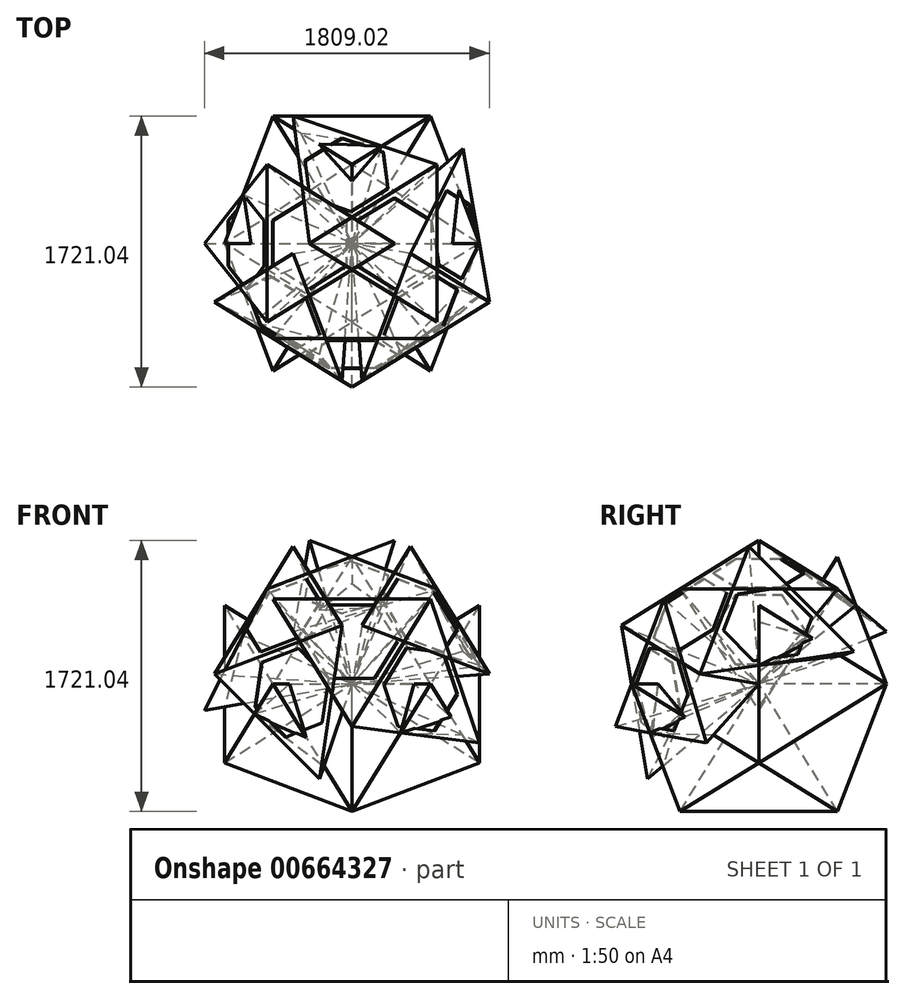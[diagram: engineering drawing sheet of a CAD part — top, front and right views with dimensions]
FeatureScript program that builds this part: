
annotation { "Feature Type Name" : "Feature", "Feature Type Description" : "" }
export const myFeature = defineFeature(function(context is Context, id is Id, definition is map)
    precondition{}
    {
        {
            var Q0;
            Q0=qCreatedBy(makeId("Front.planeOp"),FACE);
            var sketch = newSketch(context, id + "F0", { "sketchPlane" : qUnion([Q0])});
            skLineSegment(sketch, "E0.bottom", {"start": v(-809.02, 500) * mm, "end": v(190.98, 500) * mm, "construction": true});
            skLineSegment(sketch, "E0.top", {"start": v(-809.02, -500) * mm, "end": v(190.98, -500) * mm, "construction": true});
            skLineSegment(sketch, "E0.left", {"start": v(-809.02, 500) * mm, "end": v(-809.02, -500) * mm, "construction": true});
            skLineSegment(sketch, "E0.right", {"start": v(190.98, 500) * mm, "end": v(190.98, -500) * mm, "construction": true});
            skLineSegment(sketch, "E1", {"start": v(190.98, -500) * mm, "end": v(809.02, -500) * mm, "construction": true});
            skArc(sketch, "E2", {"start": v(190.98, 500) * mm, "mid": v(642.04, 87.79) * mm, "end": v(809.02, -500) * mm, "construction": true});
            skLineSegment(sketch, "E3.bottom", {"start": v(809.02, -500) * mm, "end": v(-809.02, -500) * mm});
            skLineSegment(sketch, "E3.top", {"start": v(809.02, 500) * mm, "end": v(-809.02, 500) * mm});
            skLineSegment(sketch, "E3.left", {"start": v(809.02, -500) * mm, "end": v(809.02, 500) * mm});
            skLineSegment(sketch, "E3.right", {"start": v(-809.02, -500) * mm, "end": v(-809.02, 500) * mm});
            skLineSegment(sketch, "E4", {"start": v(0, 0) * mm, "end": v(0, 500) * mm, "construction": true});
            skLineSegment(sketch, "E5", {"start": v(0, 0) * mm, "end": v(-809.02, 0) * mm, "construction": true});
            skSolve(sketch);
        }
        {
            var Q0;
            Q0=qCreatedBy(makeId("Top.planeOp"),FACE);
            var sketch = newSketch(context, id + "F1", { "sketchPlane" : qUnion([Q0])});
            skLineSegment(sketch, "E6.bottom", {"start": v(-500, -809.02) * mm, "end": v(-500, 190.98) * mm, "construction": true});
            skLineSegment(sketch, "E6.top", {"start": v(500, -809.02) * mm, "end": v(500, 190.98) * mm, "construction": true});
            skLineSegment(sketch, "E6.left", {"start": v(-500, -809.02) * mm, "end": v(500, -809.02) * mm, "construction": true});
            skLineSegment(sketch, "E6.right", {"start": v(-500, 190.98) * mm, "end": v(500, 190.98) * mm, "construction": true});
            skLineSegment(sketch, "E7", {"start": v(500, 190.98) * mm, "end": v(500, 809.02) * mm, "construction": true});
            skArc(sketch, "E8", {"start": v(-500, 190.98) * mm, "mid": v(-87.79, 642.04) * mm, "end": v(500, 809.02) * mm, "construction": true});
            skLineSegment(sketch, "E9.bottom", {"start": v(500, 809.02) * mm, "end": v(500, -809.02) * mm});
            skLineSegment(sketch, "E9.top", {"start": v(-500, 809.02) * mm, "end": v(-500, -809.02) * mm});
            skLineSegment(sketch, "E9.left", {"start": v(500, 809.02) * mm, "end": v(-500, 809.02) * mm});
            skLineSegment(sketch, "E9.right", {"start": v(500, -809.02) * mm, "end": v(-500, -809.02) * mm});
            skLineSegment(sketch, "E10", {"start": v(0, 0) * mm, "end": v(-500, 0) * mm, "construction": true});
            skLineSegment(sketch, "E11", {"start": v(0, 0) * mm, "end": v(0, -809.02) * mm, "construction": true});
            skSolve(sketch);
        }
        {
            var Q0;
            Q0=qCreatedBy(makeId("Right.planeOp"),FACE);
            var sketch = newSketch(context, id + "F2", { "sketchPlane" : qUnion([Q0])});
            skLineSegment(sketch, "E12.bottom", {"start": v(-500, -809.02) * mm, "end": v(-500, 190.98) * mm, "construction": true});
            skLineSegment(sketch, "E12.top", {"start": v(500, -809.02) * mm, "end": v(500, 190.98) * mm, "construction": true});
            skLineSegment(sketch, "E12.left", {"start": v(-500, -809.02) * mm, "end": v(500, -809.02) * mm, "construction": true});
            skLineSegment(sketch, "E12.right", {"start": v(-500, 190.98) * mm, "end": v(500, 190.98) * mm, "construction": true});
            skLineSegment(sketch, "E13", {"start": v(500, 190.98) * mm, "end": v(500, 809.02) * mm, "construction": true});
            skArc(sketch, "E14", {"start": v(-500, 190.98) * mm, "mid": v(-87.79, 642.04) * mm, "end": v(500, 809.02) * mm, "construction": true});
            skLineSegment(sketch, "E15.bottom", {"start": v(500, 809.02) * mm, "end": v(500, -809.02) * mm});
            skLineSegment(sketch, "E15.top", {"start": v(-500, 809.02) * mm, "end": v(-500, -809.02) * mm});
            skLineSegment(sketch, "E15.left", {"start": v(500, 809.02) * mm, "end": v(-500, 809.02) * mm});
            skLineSegment(sketch, "E15.right", {"start": v(500, -809.02) * mm, "end": v(-500, -809.02) * mm});
            skLineSegment(sketch, "E16", {"start": v(0, 0) * mm, "end": v(-500, 0) * mm, "construction": true});
            skLineSegment(sketch, "E17", {"start": v(0, 0) * mm, "end": v(0, -809.02) * mm, "construction": true});
            skSolve(sketch);
        }
        {
            var Q0;
            Q0=sQuery(id+"F0.wireOp",VERTEX,"E3.top.end");
            var Q1;
            Q1=sQuery(id+"F1.wireOp",VERTEX,"E6.left.start");
            var Q2;
            Q2=sQuery(id+"F2.wireOp",VERTEX,"E15.top.start");
            cPlane(context, id + "F3", {"entities" : qUnion([Q0, Q1, Q2]), "cplaneType" : CPlaneType.THREE_POINT, "offset" : 25 * mm, "width" : 150 * mm, "height" : 150 * mm});
        }
        {
            var Q0;
            Q0=qCreatedBy(id+"F3.planeOp",FACE);
            var sketch = newSketch(context, id + "F4", { "sketchPlane" : qUnion([Q0])});
            skPoint(sketch, "E18.0", {"position": v(534.4, -218.5) * mm});
            skPoint(sketch, "E19.0", {"position": v(-456.44, -353.55) * mm});
            skPoint(sketch, "E20.0", {"position": v(-77.97, 572.06) * mm});
            skLineSegment(sketch, "E21", {"start": v(-77.97, 572.06) * mm, "end": v(534.4, -218.5) * mm});
            skLineSegment(sketch, "E22", {"start": v(534.4, -218.5) * mm, "end": v(-456.44, -353.55) * mm});
            skLineSegment(sketch, "E23", {"start": v(-456.44, -353.55) * mm, "end": v(-77.97, 572.06) * mm});
            skSolve(sketch);
        }
        {
            var Q0;
            Q0=makeQuery(id+"F4.imprint","IMPRINT",FACE,{"disambiguationData":[TD([[makeQuery(id+"F4.imprint","IMPRINT",EDGE,{"derivedFrom":sQuery(id+"F4.wireOp",EDGE,"E21")}),-1.0]])]});
            var Q1;
            Q1=sQuery(id+"F1.wireOp",VERTEX,"E10.start");
            loft(context, id + "F5", {"sheetProfilesArray" : [{ "sheetProfileEntities" : qUnion([Q0]) }, { "sheetProfileEntities" : qUnion([Q1]) }]});
        }
        {
            var Q0;
            Q0=makeQuery(id+"F5.opLoft","CAP_FACE",FACE,{"disambiguationData":[OSD([makeQuery(id+"F4.imprint","IMPRINT",FACE,{"disambiguationData":[TD([[makeQuery(id+"F4.imprint","IMPRINT",EDGE,{"derivedFrom":sQuery(id+"F4.wireOp",EDGE,"E21")}),-1.0]])]})])],"isStart":true});
            var sketch = newSketch(context, id + "F6", { "sketchPlane" : qUnion([Q0])});
            skLineSegment(sketch, "E24", {"start": v(456.44, -353.55) * mm, "end": v(-228.22, 176.78) * mm, "construction": true});
            skLineSegment(sketch, "E25", {"start": v(-228.22, 176.78) * mm, "end": v(77.97, 572.06) * mm, "construction": true});
            skLineSegment(sketch, "E26", {"start": v(77.97, 572.06) * mm, "end": v(-38.98, -286.03) * mm, "construction": true});
            skLineSegment(sketch, "E27", {"start": v(-38.98, -286.03) * mm, "end": v(-534.4, -218.5) * mm, "construction": true});
            skCircle(sketch, "E28.cCircle", {"center": v(0, 0) * mm, "radius": 288.68 * mm, "construction": true});
            skLineSegment(sketch, "E28.0", {"start": v(-176.78, -228.22) * mm, "end": v(-286.03, 38.98) * mm});
            skLineSegment(sketch, "E28.1", {"start": v(-286.03, 38.98) * mm, "end": v(-109.25, 267.2) * mm});
            skLineSegment(sketch, "E28.2", {"start": v(-109.25, 267.2) * mm, "end": v(176.78, 228.22) * mm});
            skLineSegment(sketch, "E28.3", {"start": v(176.78, 228.22) * mm, "end": v(286.03, -38.98) * mm});
            skLineSegment(sketch, "E28.4", {"start": v(286.03, -38.98) * mm, "end": v(109.25, -267.2) * mm});
            skLineSegment(sketch, "E28.5", {"start": v(109.25, -267.2) * mm, "end": v(-176.78, -228.22) * mm});
            skSolve(sketch);
        }
        {
            var Q0;
            Q0 = qSketchRegion(id + "F6", true);
            extrude(context, id + "F7", {"entities" : qUnion([Q0]), "operationType" : NewBodyOperationType.REMOVE, "oppositeDirection" : true, "depth" : 5 * mm, "offsetDistance" : 25 * mm});
        }
        {
            var Q0;
            Q0=makeQuery(id+"F5.opLoft","SWEPT_BODY",BODY,{"disambiguationData":[OSD([sQuery(id+"F1.wireOp",VERTEX,"E10.start"),makeQuery(id+"F4.imprint","IMPRINT",FACE,{"disambiguationData":[TD([[makeQuery(id+"F4.imprint","IMPRINT",EDGE,{"derivedFrom":sQuery(id+"F4.wireOp",EDGE,"E21")}),-1.0]])]})])]});
            var Q1;
            {var subQ0=sQuery(id+"F4.wireOp",EDGE,"E22");var subQ1=sQuery(id+"F4.wireOp",EDGE,"E23");var subQ2=sQuery(id+"F4.wireOp",EDGE,"E21");Q1=makeQuery(id+"F5.opLoft","SWEPT_FACE",FACE,{"disambiguationData":[OSD([subQ2,subQ0,subQ1]),TDD([makeQuery(id+"F4.imprint","INTERSECT",VERTEX,{"derivedFrom":[subQ2,subQ0]}),makeQuery(id+"F4.imprint","INTERSECT",VERTEX,{"derivedFrom":[subQ0,subQ1]}),makeQuery(id+"F4.imprint","IMPRINT",EDGE,{"derivedFrom":subQ0})])]});}
            mirror(context, id + "F8", {"operationType" : NewBodyOperationType.ADD, "entities" : qUnion([Q0]), "mirrorPlane" : qUnion([Q1])});
        }
        {
            var Q0;
            Q0=sQuery(id+"F2.wireOp",VERTEX,"E15.top.end");
            var Q1;
            Q1=sQuery(id+"F0.wireOp",VERTEX,"E0.left.end");
            var Q2;
            Q2=sQuery(id+"F1.wireOp",VERTEX,"E6.left.start");
            cPlane(context, id + "F9", {"entities" : qUnion([Q0, Q1, Q2]), "cplaneType" : CPlaneType.THREE_POINT, "offset" : 25 * mm, "width" : 150 * mm, "height" : 150 * mm});
        }
        {
            var Q0;
            Q0=qCreatedBy(id+"F9.planeOp",FACE);
            var sketch = newSketch(context, id + "F10", { "sketchPlane" : qUnion([Q0])});
            skPoint(sketch, "E29.0", {"position": v(534.4, -218.5) * mm});
            skPoint(sketch, "E30.0", {"position": v(-456.44, -353.55) * mm});
            skPoint(sketch, "E31.0", {"position": v(-77.97, 572.06) * mm});
            skLineSegment(sketch, "E32", {"start": v(534.4, -218.5) * mm, "end": v(-456.44, -353.55) * mm});
            skLineSegment(sketch, "E33", {"start": v(-77.97, 572.06) * mm, "end": v(534.4, -218.5) * mm});
            skLineSegment(sketch, "E34", {"start": v(-456.44, -353.55) * mm, "end": v(-77.97, 572.06) * mm});
            skSolve(sketch);
        }
        {
            var Q1;
            Q1 = qSketchRegion(id + "F10", true);
            var Q2;
            Q2=sQuery(id+"F2.wireOp",VERTEX,"E16.start");
            loft(context, id + "F11", {"sheetProfilesArray" : [{ "sheetProfileEntities" : qUnion([Q1]) }, { "sheetProfileEntities" : qUnion([Q2]) }]});
        }
        {
            var Q0;
            Q0=makeQuery(id+"F11.opLoft","SWEPT_BODY",BODY,{"disambiguationData":[OSD([sQuery(id+"F2.wireOp",VERTEX,"E16.start"),makeQuery(id+"F10.imprint","IMPRINT",FACE,{"disambiguationData":[TD([[makeQuery(id+"F10.imprint","IMPRINT",EDGE,{"derivedFrom":sQuery(id+"F10.wireOp",EDGE,"E32")}),-1.0]])]})])]});
            var Q1;
            {var subQ0=sQuery(id+"F10.wireOp",EDGE,"E32");var subQ1=sQuery(id+"F10.wireOp",EDGE,"E34");var subQ2=sQuery(id+"F10.wireOp",EDGE,"E33");Q1=makeQuery(id+"F11.opLoft","SWEPT_FACE",FACE,{"disambiguationData":[OSD([subQ0,subQ2,subQ1]),TDD([makeQuery(id+"F10.imprint","INTERSECT",VERTEX,{"derivedFrom":[subQ0,subQ2]}),makeQuery(id+"F10.imprint","INTERSECT",VERTEX,{"derivedFrom":[subQ0,subQ1]}),makeQuery(id+"F10.imprint","IMPRINT",EDGE,{"derivedFrom":subQ0})])]});}
            mirror(context, id + "F12", {"operationType" : NewBodyOperationType.ADD, "entities" : qUnion([Q0]), "mirrorPlane" : qUnion([Q1])});
        }
        {
            var Q0;
            Q0=makeQuery(id+"F5.opLoft","SWEPT_BODY",BODY,{"disambiguationData":[OSD([sQuery(id+"F1.wireOp",VERTEX,"E10.start"),makeQuery(id+"F4.imprint","IMPRINT",FACE,{"disambiguationData":[TD([[makeQuery(id+"F4.imprint","IMPRINT",EDGE,{"derivedFrom":sQuery(id+"F4.wireOp",EDGE,"E21")}),-1.0]])]})])]});
            var Q1;
            Q1=makeQuery(id+"F11.opLoft","SWEPT_BODY",BODY,{"disambiguationData":[OSD([sQuery(id+"F2.wireOp",VERTEX,"E16.start"),makeQuery(id+"F10.imprint","IMPRINT",FACE,{"disambiguationData":[TD([[makeQuery(id+"F10.imprint","IMPRINT",EDGE,{"derivedFrom":sQuery(id+"F10.wireOp",EDGE,"E32")}),-1.0]])]})])]});
            var Q2;
            Q2=makeQuery(id+"F12.opPattern","COPY",EDGE,{"derivedFrom":makeQuery(id+"F11.opLoft","SWEPT_EDGE",EDGE,{"disambiguationData":[OSD([sQuery(id+"F2.wireOp",VERTEX,"E16.start"),sQuery(id+"F10.wireOp",EDGE,"E33"),sQuery(id+"F10.wireOp",EDGE,"E34")])]}),"instanceName":"1"});
            circularPattern(context, id + "F13", {"entities" : qUnion([Q0, Q1]), "axis" : qUnion([Q2]), "angle" : 360 * degree, "instanceCount" : 5, "equalSpace" : true});
        }
    });
